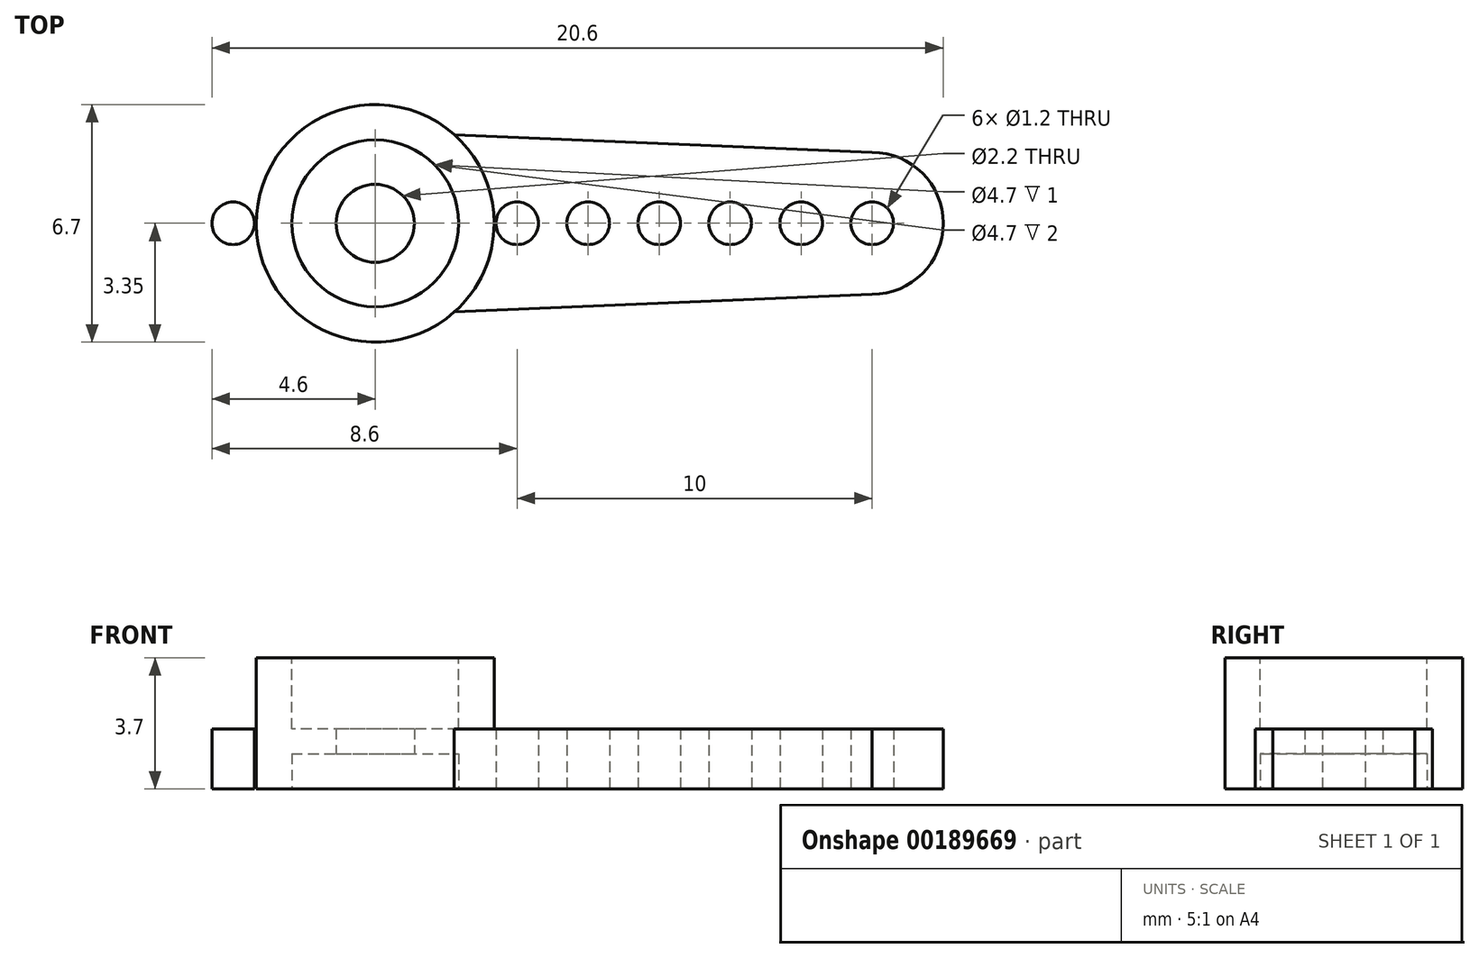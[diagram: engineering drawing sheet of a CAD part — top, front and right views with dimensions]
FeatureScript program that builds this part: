
annotation { "Feature Type Name" : "Feature", "Feature Type Description" : "" }
export const myFeature = defineFeature(function(context is Context, id is Id, definition is map)
    precondition{}
    {
        {
            var Q0;
            Q0=qCreatedBy(makeId("Top.planeOp"),FACE);
            var sketch = newSketch(context, id + "F0", { "sketchPlane" : qUnion([Q0])});
            skCircle(sketch, "E0", {"center": v(0, 0) * mm, "radius": 3.35 * mm});
            skCircle(sketch, "E1", {"center": v(6, 0) * mm, "radius": 0.6 * mm});
            skCircle(sketch, "E2.1.0.0", {"center": v(8, 0) * mm, "radius": 0.6 * mm});
            skCircle(sketch, "E2.2.0.0", {"center": v(10, 0) * mm, "radius": 0.6 * mm});
            skCircle(sketch, "E2.3.0.0", {"center": v(12, 0) * mm, "radius": 0.6 * mm});
            skCircle(sketch, "E2.4.0.0", {"center": v(14, 0) * mm, "radius": 0.6 * mm});
            skLineSegment(sketch, "E2.direction1", {"start": v(6, 0) * mm, "end": v(8, 0) * mm, "construction": true});
            skCircle(sketch, "E3.1.0.0", {"center": v(4, 0) * mm, "radius": 0.6 * mm});
            skLineSegment(sketch, "E3.direction1", {"start": v(6, 0) * mm, "end": v(4, 0) * mm, "construction": true});
            skLineSegment(sketch, "E4", {"start": v(2.23, 2.5) * mm, "end": v(14, 2) * mm});
            skLineSegment(sketch, "E5", {"start": v(0, 0) * mm, "end": v(1.18, 0) * mm, "construction": true});
            skLineSegment(sketch, "E6", {"start": v(2.23, -2.5) * mm, "end": v(14, -2) * mm});
            skArc(sketch, "E7", {"start": v(14, 2) * mm, "mid": v(16, 0) * mm, "end": v(14, -2) * mm});
            skLineSegment(sketch, "E8", {"start": v(0, 0) * mm, "end": v(0, 1.94) * mm, "construction": true});
            skCircle(sketch, "E9.MirrorC", {"center": v(-4, 0) * mm, "radius": 0.6 * mm});
            skCircle(sketch, "E10.MirrorC", {"center": v(-6, 0) * mm, "radius": 0.6 * mm});
            skCircle(sketch, "E11.MirrorC", {"center": v(-8, 0) * mm, "radius": 0.6 * mm});
            skCircle(sketch, "E12.MirrorC", {"center": v(-10, 0) * mm, "radius": 0.6 * mm});
            skCircle(sketch, "E13.MirrorC", {"center": v(-12, 0) * mm, "radius": 0.6 * mm});
            skCircle(sketch, "E14.MirrorC", {"center": v(-14, 0) * mm, "radius": 0.6 * mm});
            skLineSegment(sketch, "E15.MirrorCS", {"start": v(-2.23, 2.5) * mm, "end": v(-14, 2) * mm});
            skLineSegment(sketch, "E16.MirrorCS", {"start": v(-2.23, -2.5) * mm, "end": v(-14, -2) * mm});
            skArc(sketch, "E17.MirrorCS", {"start": v(-14, 2) * mm, "mid": v(-16, 0) * mm, "end": v(-14, -2) * mm});
            skLineSegment(sketch, "E18", {"start": v(-9.17, 2.2) * mm, "end": v(-9.17, -2.2) * mm});
            skSolve(sketch);
        }
        {
            var Q0;
            {var subQ0=sQuery(id+"F0.wireOp",EDGE,"E0");var subQ1=makeQuery(id+"F0.imprint","INTERSECT",VERTEX,{"derivedFrom":[subQ0,sQuery(id+"F0.wireOp",EDGE,"E4")]});Q0=makeQuery(id+"F0.imprint","IMPRINT",FACE,{"disambiguationData":[TD([[makeQuery(id+"F0.imprint","IMPRINT",EDGE,{"disambiguationData":[TD([[subQ1,-1.0]])],"derivedFrom":subQ0}),1.0]])]});}
            var Q1;
            Q1=makeQuery(id+"F0.imprint","IMPRINT",FACE,{"disambiguationData":[TD([[makeQuery(id+"F0.imprint","IMPRINT",EDGE,{"derivedFrom":sQuery(id+"F0.wireOp",EDGE,"E1")}),-1.0]])]});
            var Q2;
            Q2=makeQuery(id+"F0.imprint","IMPRINT",FACE,{"disambiguationData":[TD([[makeQuery(id+"F0.imprint","IMPRINT",EDGE,{"derivedFrom":sQuery(id+"F0.wireOp",EDGE,"E9.MirrorC")}),1.0]])]});
            extrude(context, id + "F1", {"entities" : qUnion([Q0, Q1, Q2]), "depth" : 1.7 * mm});
        }
        {
            var Q0;
            Q0=makeQuery(id+"F1.opExtrude","CAP_FACE",FACE,{"disambiguationData":[OSD([sQuery(id+"F0.wireOp",EDGE,"E0"),sQuery(id+"F0.wireOp",EDGE,"E1"),sQuery(id+"F0.wireOp",EDGE,"E2.1.0.0"),sQuery(id+"F0.wireOp",EDGE,"E2.2.0.0"),sQuery(id+"F0.wireOp",EDGE,"E2.3.0.0"),sQuery(id+"F0.wireOp",EDGE,"E2.4.0.0"),sQuery(id+"F0.wireOp",EDGE,"E3.1.0.0"),sQuery(id+"F0.wireOp",EDGE,"E4"),sQuery(id+"F0.wireOp",EDGE,"E6"),sQuery(id+"F0.wireOp",EDGE,"4d52fdd3-3aff-440c-9459-d1f9478f26ee")])],"isStart":false});
            var sketch = newSketch(context, id + "F2", { "sketchPlane" : qUnion([Q0])});
            skCircle(sketch, "E19", {"center": v(0, 0) * mm, "radius": 3.35 * mm});
            skSolve(sketch);
        }
        {
            var Q0;
            {var subQ0=sQuery(id+"F2.wireOp",EDGE,"E19");var subQ1=makeQuery(id+"F2.imprint","INTERSECT",VERTEX,{"derivedFrom":[makeQuery(id+"F1.opExtrude","CAP_EDGE",EDGE,{"disambiguationData":[OSD([sQuery(id+"F0.wireOp",EDGE,"E4")])],"isStart":false}),subQ0]});Q0=makeQuery(id+"F2.imprint","IMPRINT",FACE,{"disambiguationData":[TD([[makeQuery(id+"F2.imprint","IMPRINT",EDGE,{"disambiguationData":[TD([[subQ1,-1.0]])],"derivedFrom":subQ0}),1.0]])]});}
            extrude(context, id + "F3", {"entities" : qUnion([Q0]), "operationType" : NewBodyOperationType.ADD, "depth" : 2 * mm});
        }
        {
            var Q0;
            Q0=makeQuery(id+"F1.opExtrude","CAP_FACE",FACE,{"disambiguationData":[OSD([sQuery(id+"F0.wireOp",EDGE,"E0"),sQuery(id+"F0.wireOp",EDGE,"E1"),sQuery(id+"F0.wireOp",EDGE,"E2.1.0.0"),sQuery(id+"F0.wireOp",EDGE,"E2.2.0.0"),sQuery(id+"F0.wireOp",EDGE,"E2.3.0.0"),sQuery(id+"F0.wireOp",EDGE,"E2.4.0.0"),sQuery(id+"F0.wireOp",EDGE,"E3.1.0.0"),sQuery(id+"F0.wireOp",EDGE,"E4"),sQuery(id+"F0.wireOp",EDGE,"E6"),sQuery(id+"F0.wireOp",EDGE,"4d52fdd3-3aff-440c-9459-d1f9478f26ee")])],"isStart":true});
            var sketch = newSketch(context, id + "F4", { "sketchPlane" : qUnion([Q0])});
            skLineSegment(sketch, "E20.0", {"start": v(2.23, -2.5) * mm, "end": v(2.23, -2.5) * mm});
            skArc(sketch, "E21.0", {"start": v(1.56, -1.75) * mm, "mid": v(-2.35, 0) * mm, "end": v(1.56, 1.75) * mm});
            skArc(sketch, "E22", {"start": v(1.56, -1.75) * mm, "mid": v(2.35, 0) * mm, "end": v(1.56, 1.75) * mm});
            skSolve(sketch);
        }
        {
            var Q0;
            Q0=qSketchRegion(id+"F4",true);
            extrude(context, id + "F5", {"entities" : qUnion([Q0]), "operationType" : NewBodyOperationType.REMOVE, "oppositeDirection" : true, "depth" : 1 * mm});
        }
        {
            var Q0;
            Q0=makeQuery(id+"F5.boolean.opBoolean","COPY",FACE,{"derivedFrom":makeQuery(id+"F5.opExtrude","CAP_FACE",FACE,{"disambiguationData":[OSD([sQuery(id+"F4.wireOp",EDGE,"E21.0"),sQuery(id+"F4.wireOp",EDGE,"E22")])],"isStart":false})});
            var sketch = newSketch(context, id + "F6", { "sketchPlane" : qUnion([Q0])});
            skCircle(sketch, "E23", {"center": v(0, 0) * mm, "radius": 1.1 * mm});
            skSolve(sketch);
        }
        {
            var Q0;
            Q0=makeQuery(id+"F6.imprint","IMPRINT",FACE,{"disambiguationData":[TD([[makeQuery(id+"F6.imprint","IMPRINT",EDGE,{"derivedFrom":sQuery(id+"F6.wireOp",EDGE,"E23")}),1.0]])]});
            extrude(context, id + "F7", {"entities" : qUnion([Q0]), "operationType" : NewBodyOperationType.REMOVE, "endBound" : BoundingType.THROUGH_ALL, "oppositeDirection" : true, "depth" : 25 * mm});
        }
        {
            var Q0;
            Q0=makeQuery(id+"F3.opExtrude","CAP_FACE",FACE,{"disambiguationData":[OSD([sQuery(id+"F2.wireOp",EDGE,"E19")])],"isStart":false});
            var sketch = newSketch(context, id + "F8", { "sketchPlane" : qUnion([Q0])});
            skCircle(sketch, "E24.0", {"center": v(0, 0) * mm, "radius": 3.35 * mm});
            skCircle(sketch, "E25.0", {"center": v(0, 0) * mm, "radius": 2.35 * mm});
            skCircle(sketch, "E26.0", {"center": v(0, 0) * mm, "radius": 8.35 * mm});
            skSolve(sketch);
        }
        {
            var Q0;
            Q0=makeQuery(id+"F8.imprint","IMPRINT",FACE,{"disambiguationData":[TD([[makeQuery(id+"F8.imprint","IMPRINT",EDGE,{"derivedFrom":sQuery(id+"F8.wireOp",EDGE,"E25.0")}),1.0]])]});
            var Q1;
            {var subQ0=sQuery(id+"F0.wireOp",EDGE,"E16.MirrorCS");var subQ1=sQuery(id+"F0.wireOp",EDGE,"E15.MirrorCS");var subQ2=sQuery(id+"F0.wireOp",EDGE,"E9.MirrorC");var subQ3=sQuery(id+"F0.wireOp",EDGE,"E14.MirrorC");var subQ4=sQuery(id+"F0.wireOp",EDGE,"E13.MirrorC");var subQ5=sQuery(id+"F0.wireOp",EDGE,"E12.MirrorC");var subQ6=sQuery(id+"F0.wireOp",EDGE,"E11.MirrorC");var subQ7=sQuery(id+"F0.wireOp",EDGE,"E4");var subQ8=sQuery(id+"F0.wireOp",EDGE,"E0");var subQ9=sQuery(id+"F0.wireOp",EDGE,"E10.MirrorC");var subQ10=sQuery(id+"F0.wireOp",EDGE,"E17.MirrorCS");var subQ11=sQuery(id+"F0.wireOp",EDGE,"E6");Q1=makeQuery(id+"F3.boolean.opBoolean","SPLIT",FACE,{"disambiguationData":[TD([makeQuery(id+"F1.opExtrude","SWEPT_FACE",FACE,{"disambiguationData":[OSD([subQ2])]})])],"derivedFrom":makeQuery(id+"F1.opExtrude","CAP_FACE",FACE,{"disambiguationData":[OSD([subQ8,sQuery(id+"F0.wireOp",EDGE,"E1"),sQuery(id+"F0.wireOp",EDGE,"E2.1.0.0"),sQuery(id+"F0.wireOp",EDGE,"E2.2.0.0"),sQuery(id+"F0.wireOp",EDGE,"E2.3.0.0"),sQuery(id+"F0.wireOp",EDGE,"E2.4.0.0"),sQuery(id+"F0.wireOp",EDGE,"E3.1.0.0"),subQ7,subQ11,sQuery(id+"F0.wireOp",EDGE,"E7"),subQ2,subQ9,subQ6,subQ5,subQ4,subQ3,subQ1,subQ0,subQ10])],"isStart":false})});}
            extrude(context, id + "F9", {"entities" : qUnion([Q0]), "operationType" : NewBodyOperationType.REMOVE, "endBound" : BoundingType.UP_TO_SURFACE, "oppositeDirection" : true, "endBoundEntityFace" : qUnion([Q1]), "depth" : 25 * mm});
        }
    });
